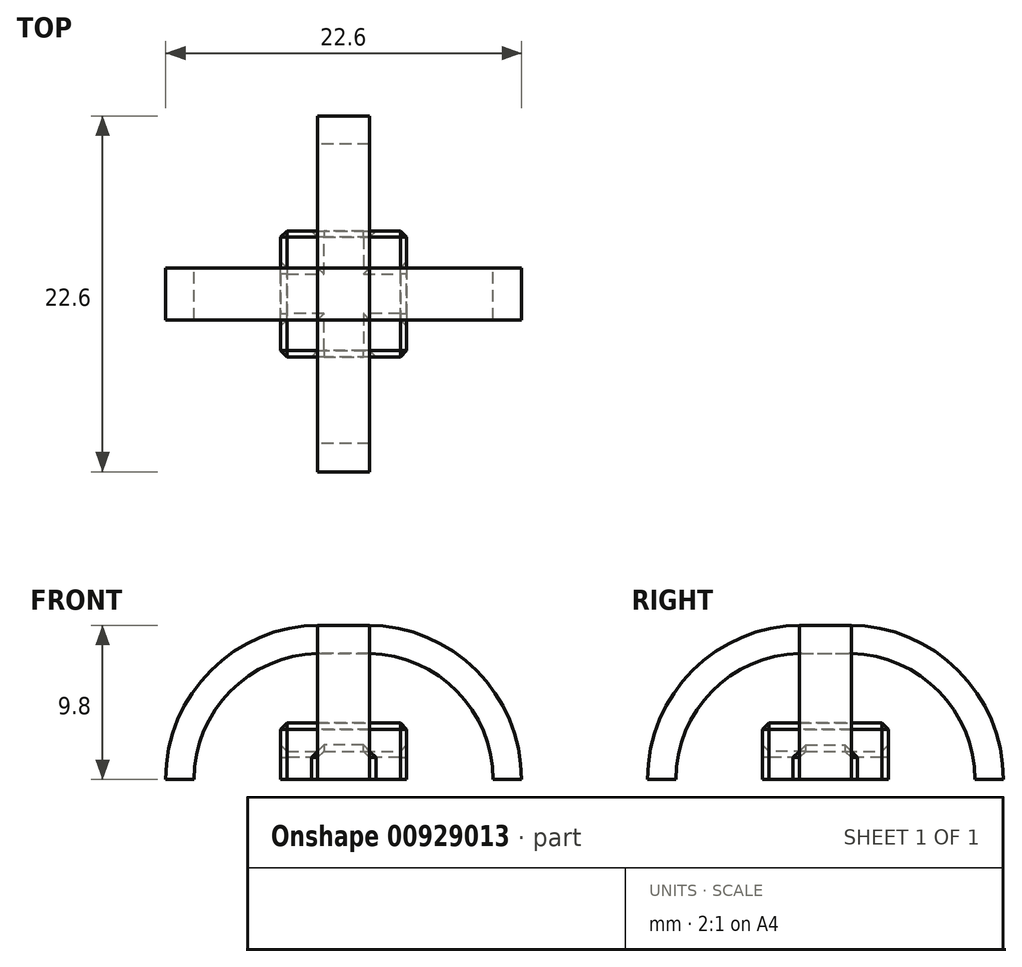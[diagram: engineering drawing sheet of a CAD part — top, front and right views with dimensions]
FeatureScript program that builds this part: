
annotation { "Feature Type Name" : "Feature", "Feature Type Description" : "" }
export const myFeature = defineFeature(function(context is Context, id is Id, definition is map)
    precondition{}
    {
        {
            assignVariable(context, id + "F0", {"name" : "width", "anyValue" : 3.3 * mm});
        }
        {
            assignVariable(context, id + "F1", {"name" : "thickness", "anyValue" : 1.8 * mm});
        }
        {
            var Q0;
            Q0=qCreatedBy(makeId("Front.planeOp"),FACE);
            var sketch = newSketch(context, id + "F2", { "sketchPlane" : qUnion([Q0])});
            skLineSegment(sketch, "E0", {"start": v(0, 0) * mm, "end": v(0, 8) * mm, "construction": true});
            skLineSegment(sketch, "E1", {"start": v(-0.15, 9.8) * mm, "end": v(1.5, 9.8) * mm});
            skLineSegment(sketch, "E2", {"start": v(1.5, 8) * mm, "end": v(0, 8) * mm});
            skLineSegment(sketch, "E3", {"start": v(1.5, 8) * mm, "end": v(1.5, 0) * mm, "construction": true});
            skArc(sketch, "E4", {"start": v(9.5, 0) * mm, "mid": v(7.16, 5.66) * mm, "end": v(1.5, 8) * mm});
            skArc(sketch, "E5", {"start": v(11.3, 0) * mm, "mid": v(8.43, 6.93) * mm, "end": v(1.5, 9.8) * mm});
            skLineSegment(sketch, "E6", {"start": v(9.5, 0) * mm, "end": v(11.3, 0) * mm});
            skLineSegment(sketch, "E7.MirrorCS", {"start": v(-1.5, 8) * mm, "end": v(0, 8) * mm});
            skArc(sketch, "E8.MirrorCS", {"start": v(-9.5, 0) * mm, "mid": v(-7.16, 5.66) * mm, "end": v(-1.5, 8) * mm});
            skArc(sketch, "E9.MirrorCS", {"start": v(-11.3, 0) * mm, "mid": v(-8.43, 6.93) * mm, "end": v(-1.5, 9.8) * mm});
            skLineSegment(sketch, "E10.MirrorCS", {"start": v(-9.5, 0) * mm, "end": v(-11.3, 0) * mm});
            skLineSegment(sketch, "E11.MirrorCS", {"start": v(0.15, 9.8) * mm, "end": v(-1.5, 9.8) * mm});
            skSolve(sketch);
        }
        {
            var Q0;
            Q0 = qSketchRegion(id + "F2", true);
            extrude(context, id + "F3", {"entities" : qUnion([Q0]), "endBound" : BoundingType.SYMMETRIC, "depth" : getVariable(context, 'width'), "offsetDistance" : 25 * mm});
        }
        {
            var Q0;
            Q0=makeQuery(id+"F3.opExtrude","SWEPT_BODY",BODY,{"disambiguationData":[OSD([sQuery(id+"F2.wireOp",EDGE,"E1"),sQuery(id+"F2.wireOp",EDGE,"E2"),sQuery(id+"F2.wireOp",EDGE,"E4"),sQuery(id+"F2.wireOp",EDGE,"E5"),sQuery(id+"F2.wireOp",EDGE,"E6"),sQuery(id+"F2.wireOp",EDGE,"E7.MirrorCS"),sQuery(id+"F2.wireOp",EDGE,"E8.MirrorCS"),sQuery(id+"F2.wireOp",EDGE,"E9.MirrorCS"),sQuery(id+"F2.wireOp",EDGE,"E10.MirrorCS"),sQuery(id+"F2.wireOp",EDGE,"E11.MirrorCS")])]});
            var Q1;
            Q1=sQuery(id+"F2.wireOp",EDGE,"E0");
            transform(context, id + "F4", {"entities" : qUnion([Q0]), "transformType" : TransformType.ROTATION, "transformAxis" : qUnion([Q1]), "angle" : 90 * degree, "makeCopy" : true});
        }
        {
            var Q0;
            Q0=qCreatedBy(makeId("Top.planeOp"),FACE);
            var sketch = newSketch(context, id + "F5", { "sketchPlane" : qUnion([Q0])});
            skLineSegment(sketch, "E12.bottom", {"start": v(4, 4) * mm, "end": v(-4, 4) * mm});
            skLineSegment(sketch, "E12.top", {"start": v(4, -4) * mm, "end": v(-4, -4) * mm});
            skLineSegment(sketch, "E12.left", {"start": v(4, 4) * mm, "end": v(4, -4) * mm});
            skLineSegment(sketch, "E12.right", {"start": v(-4, 4) * mm, "end": v(-4, -4) * mm});
            skPoint(sketch, "E12.middle", {"position": v(0, 0) * mm});
            skLineSegment(sketch, "E13.bottom", {"start": v(1.65, 4) * mm, "end": v(-1.65, 4) * mm});
            skLineSegment(sketch, "E13.top", {"start": v(1.65, -4) * mm, "end": v(-1.65, -4) * mm});
            skLineSegment(sketch, "E13.left", {"start": v(1.65, 4) * mm, "end": v(1.65, 1.65) * mm});
            skLineSegment(sketch, "E13.right", {"start": v(-1.65, 4) * mm, "end": v(-1.65, 1.65) * mm});
            skLineSegment(sketch, "E14.bottom", {"start": v(4, 1.65) * mm, "end": v(1.65, 1.65) * mm});
            skLineSegment(sketch, "E14.top", {"start": v(4, -1.65) * mm, "end": v(1.65, -1.65) * mm});
            skLineSegment(sketch, "E14.left", {"start": v(4, 1.65) * mm, "end": v(4, -1.65) * mm});
            skLineSegment(sketch, "E14.right", {"start": v(-4, 1.65) * mm, "end": v(-4, -1.65) * mm});
            skPoint(sketch, "E15", {"position": v(-1.65, 1.65) * mm});
            skPoint(sketch, "E16", {"position": v(1.65, 1.65) * mm});
            skPoint(sketch, "E17", {"position": v(1.65, -1.5) * mm});
            skPoint(sketch, "E18", {"position": v(-1.65, -1.65) * mm});
            skLineSegment(sketch, "E19.trimOffspring", {"start": v(-1.65, 1.65) * mm, "end": v(-4, 1.65) * mm});
            skLineSegment(sketch, "E20.trimOffspring", {"start": v(1.65, -1.5) * mm, "end": v(1.65, -4) * mm});
            skLineSegment(sketch, "E21.trimOffspring", {"start": v(-1.65, -1.65) * mm, "end": v(-1.65, -4) * mm});
            skLineSegment(sketch, "E22.trimOffspring", {"start": v(-1.65, -1.65) * mm, "end": v(-4, -1.65) * mm});
            skSolve(sketch);
        }
        {
            var Q0;
            Q0 = qSketchRegion(id + "F5", true);
            extrude(context, id + "F6", {"entities" : qUnion([Q0]), "depth" : getVariable(context, 'thickness') * 2, "offsetDistance" : 25 * mm, "hasSecondDirection" : true, "secondDirectionOppositeDirection" : false, "secondDirectionDepth" : getVariable(context, 'thickness')});
        }
        {
            var Q0;
            {var subQ3=sQuery(id+"F5.wireOp",EDGE,"E13.right");Q0=makeQuery(id+"F5.imprint","IMPRINT",FACE,{"disambiguationData":[TD([[makeQuery(id+"F5.imprint","IMPRINT",EDGE,{"derivedFrom":subQ3}),-1.0]])]});}
            var Q1;
            {var subQ3=sQuery(id+"F5.wireOp",EDGE,"E13.left");Q1=makeQuery(id+"F5.imprint","IMPRINT",FACE,{"disambiguationData":[TD([[makeQuery(id+"F5.imprint","IMPRINT",EDGE,{"derivedFrom":subQ3}),1.0]])]});}
            var Q2;
            {var subQ5=sQuery(id+"F5.wireOp",EDGE,"E14.top");Q2=makeQuery(id+"F5.imprint","IMPRINT",FACE,{"disambiguationData":[TD([[makeQuery(id+"F5.imprint","IMPRINT",EDGE,{"derivedFrom":subQ5}),1.0]])]});}
            var Q3;
            {var subQ3=sQuery(id+"F5.wireOp",EDGE,"E21.trimOffspring");Q3=makeQuery(id+"F5.imprint","IMPRINT",FACE,{"disambiguationData":[TD([[makeQuery(id+"F5.imprint","IMPRINT",EDGE,{"derivedFrom":subQ3}),-1.0]])]});}
            extrude(context, id + "F7", {"entities" : qUnion([Q0, Q1, Q2, Q3]), "operationType" : NewBodyOperationType.ADD, "depth" : getVariable(context, 'thickness'), "offsetDistance" : 25 * mm});
        }
        {
            var Q0;
            {var subQ0=sQuery(id+"F5.wireOp",EDGE,"E12.right");var subQ1=sQuery(id+"F5.wireOp",EDGE,"E12.top");Q0=makeQuery(id+"F7.boolean.opBoolean","MERGE",EDGE,{"derivedFrom":[makeQuery(id+"F6.opExtrude","SWEPT_EDGE",EDGE,{"disambiguationData":[OSD([subQ1,subQ0])]}),makeQuery(id+"F7.opExtrude","SWEPT_EDGE",EDGE,{"disambiguationData":[OSD([subQ1,subQ0])]})]});}
            var Q1;
            {var subQ0=sQuery(id+"F5.wireOp",EDGE,"E12.right");var subQ1=sQuery(id+"F5.wireOp",EDGE,"E12.bottom");Q1=makeQuery(id+"F7.boolean.opBoolean","MERGE",EDGE,{"derivedFrom":[makeQuery(id+"F6.opExtrude","SWEPT_EDGE",EDGE,{"disambiguationData":[OSD([subQ1,subQ0])]}),makeQuery(id+"F7.opExtrude","SWEPT_EDGE",EDGE,{"disambiguationData":[OSD([subQ1,subQ0])]})]});}
            var Q2;
            {var subQ0=sQuery(id+"F5.wireOp",EDGE,"E12.left");var subQ1=sQuery(id+"F5.wireOp",EDGE,"E12.bottom");Q2=makeQuery(id+"F7.boolean.opBoolean","MERGE",EDGE,{"derivedFrom":[makeQuery(id+"F6.opExtrude","SWEPT_EDGE",EDGE,{"disambiguationData":[OSD([subQ1,subQ0])]}),makeQuery(id+"F7.opExtrude","SWEPT_EDGE",EDGE,{"disambiguationData":[OSD([subQ1,subQ0])]})]});}
            var Q3;
            {var subQ0=sQuery(id+"F5.wireOp",EDGE,"E12.left");var subQ1=sQuery(id+"F5.wireOp",EDGE,"E12.top");Q3=makeQuery(id+"F7.boolean.opBoolean","MERGE",EDGE,{"derivedFrom":[makeQuery(id+"F6.opExtrude","SWEPT_EDGE",EDGE,{"disambiguationData":[OSD([subQ1,subQ0])]}),makeQuery(id+"F7.opExtrude","SWEPT_EDGE",EDGE,{"disambiguationData":[OSD([subQ1,subQ0])]})]});}
            var Q4;
            Q4=makeQuery(id+"F6.opExtrude","CAP_FACE",FACE,{"disambiguationData":[OSD([sQuery(id+"F5.wireOp",EDGE,"E12.bottom"),sQuery(id+"F5.wireOp",EDGE,"E12.top"),sQuery(id+"F5.wireOp",EDGE,"E12.left"),sQuery(id+"F5.wireOp",EDGE,"E12.right"),sQuery(id+"F5.wireOp",EDGE,"E13.bottom"),sQuery(id+"F5.wireOp",EDGE,"E13.top"),sQuery(id+"F5.wireOp",EDGE,"E14.left"),sQuery(id+"F5.wireOp",EDGE,"E14.right")])],"isStart":false});
            var Q5;
            Q5=makeQuery(id+"F6.opExtrude","CAP_FACE",FACE,{"disambiguationData":[OSD([sQuery(id+"F5.wireOp",EDGE,"E12.bottom"),sQuery(id+"F5.wireOp",EDGE,"E12.top"),sQuery(id+"F5.wireOp",EDGE,"E12.left"),sQuery(id+"F5.wireOp",EDGE,"E12.right"),sQuery(id+"F5.wireOp",EDGE,"E13.bottom"),sQuery(id+"F5.wireOp",EDGE,"E13.top"),sQuery(id+"F5.wireOp",EDGE,"E14.left"),sQuery(id+"F5.wireOp",EDGE,"E14.right")])],"isStart":true});
            chamfer(context, id + "F8", {"entities" : qUnion([Q0, Q1, Q2, Q3, Q4, Q5]), "width" : 0.4 * mm, "tangentPropagation" : true});
        }
    });
